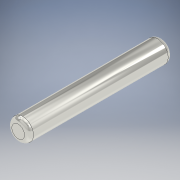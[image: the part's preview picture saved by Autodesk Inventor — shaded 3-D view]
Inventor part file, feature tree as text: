
AUTODESK INVENTOR PART (.ipt)
format: ipt  version: 2021 (Build 250183000, 183)  size: 1,092,096 bytes
history: native  units: mm
features: sketch x2, extrude x1, fillet x1, emboss x1
ambient origin geometry x8: Origin, YZ Plane, XZ Plane, XY Plane, X Axis, Y Axis, Z Axis, Center Point
bodies: Solid1 (feature_tree)
feature tree (5):
  extrude  "Extrusion1"  Depth=5.0mm TaperAngle=0.0deg
  fillet  "Fillet1"  Radius=5.0mm
  emboss  "Emboss1"
  sketch  "Sketch1"  dims[d0=24.181mm d1=160.0mm d2=0.0mm d3=5.0mm]
  sketch  "Sketch2"  dims[d5=15.0mm d6=5.0mm d7=0.0mm]
